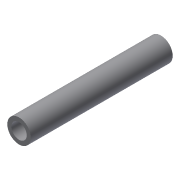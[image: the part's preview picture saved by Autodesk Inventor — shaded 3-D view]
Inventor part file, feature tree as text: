
AUTODESK INVENTOR PART (.ipt)
format: ipt  version: 2018 (Build 220112000, 112)  size: 97,792 bytes
history: native  units: mm
features: extrude x1, sketch x1
ambient origin geometry x8: Origin, YZ Plane, XZ Plane, XY Plane, X Axis, Y Axis, Z Axis, Center Point
bodies: Volumenkörper1 (feature_tree)
feature tree (2):
  extrude  "Extrusion1"  Depth=35.0mm
  sketch  "Skizze1"  dims[d0=3.8mm d1=1.0mm d2=35.0mm d3=0.0mm]
